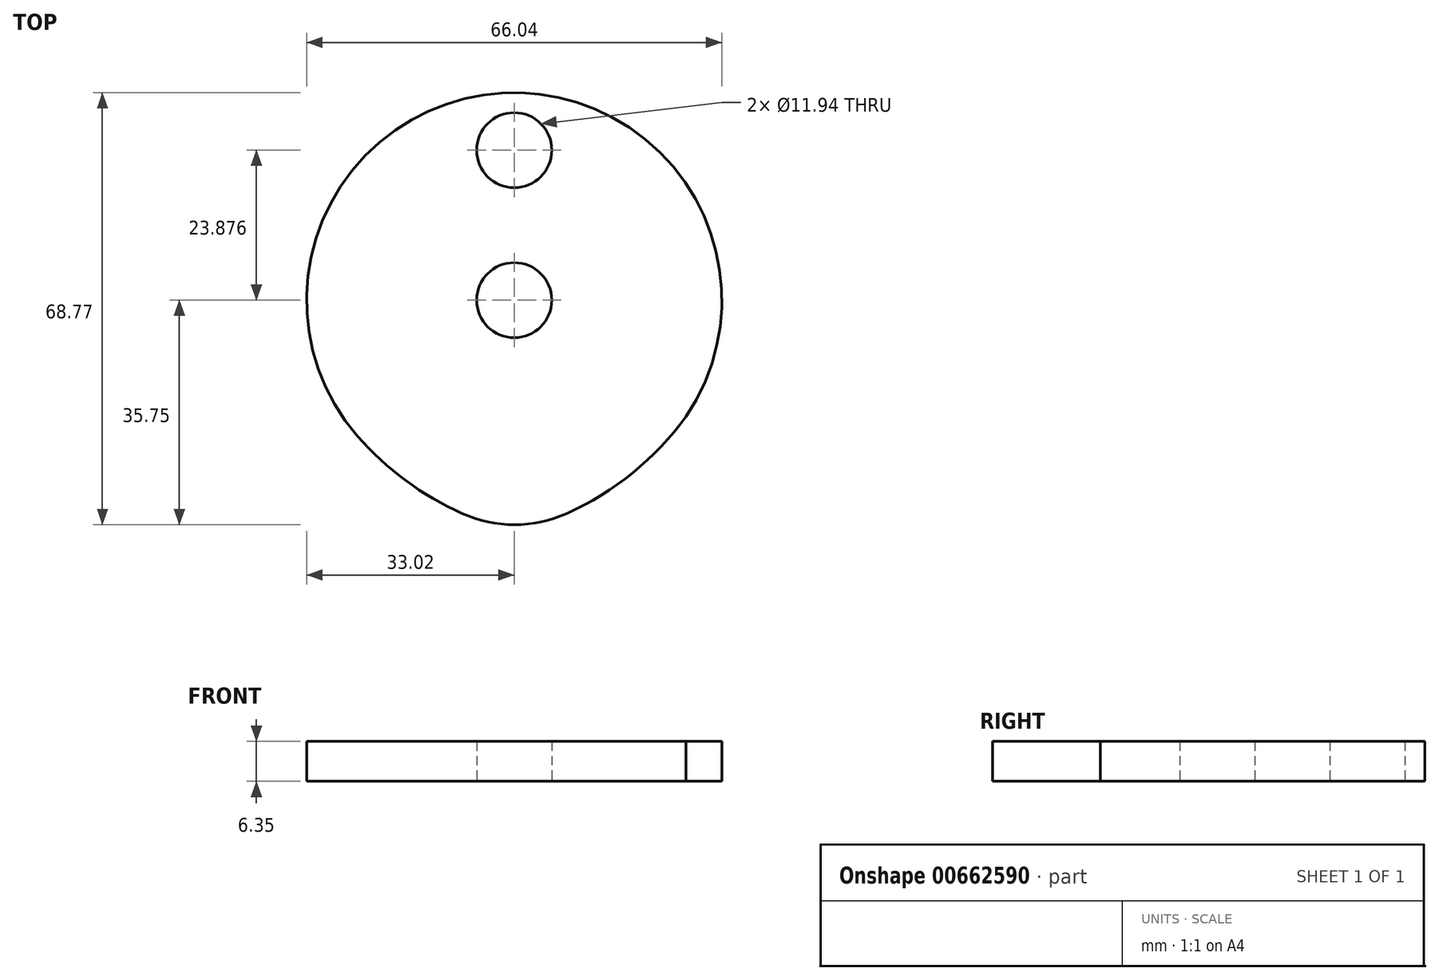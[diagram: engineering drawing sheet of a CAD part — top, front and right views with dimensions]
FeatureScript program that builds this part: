
annotation { "Feature Type Name" : "Feature", "Feature Type Description" : "" }
export const myFeature = defineFeature(function(context is Context, id is Id, definition is map)
    precondition{}
    {
        {
            var Q0;
            Q0=qCreatedBy(makeId("Top.planeOp"),FACE);
            var sketch = newSketch(context, id + "F0", { "sketchPlane" : qUnion([Q0])});
            skArc(sketch, "E0", {"start": v(27.31, -18.56) * mm, "mid": v(-1.96, 32.96) * mm, "end": v(-24.92, -21.66) * mm});
            skLineSegment(sketch, "E1", {"start": v(0, -33.02) * mm, "end": v(0, 23.88) * mm});
            skCircle(sketch, "E2", {"center": v(0, 23.88) * mm, "radius": 5.97 * mm});
            skCircle(sketch, "E3", {"center": v(0, 0) * mm, "radius": 5.97 * mm});
            skLineSegment(sketch, "E4", {"start": v(0, -33.02) * mm, "end": v(0, -36.83) * mm});
            skArc(sketch, "E5", {"start": v(-24.92, -21.66) * mm, "mid": v(-13.62, -31.15) * mm, "end": v(0, -36.83) * mm});
            skArc(sketch, "E6", {"start": v(0, -36.83) * mm, "mid": v(15.3, -30.14) * mm, "end": v(27.31, -18.56) * mm});
            skSolve(sketch);
        }
        {
            var Q0;
            Q0=makeQuery(id+"F0.imprint","IMPRINT",FACE,{"disambiguationData":[TD([[makeQuery(id+"F0.imprint","IMPRINT",EDGE,{"derivedFrom":sQuery(id+"F0.wireOp",EDGE,"E0")}),1.0]])]});
            extrude(context, id + "F1", {"entities" : qUnion([Q0]), "depth" : 6.35 * mm, "offsetDistance" : 25.4 * mm});
        }
        {
            var Q0;
            Q0=makeQuery(id+"F1.opExtrude","SWEPT_EDGE",EDGE,{"disambiguationData":[OSD([sQuery(id+"F0.wireOp",EDGE,"E5"),sQuery(id+"F0.wireOp",EDGE,"E6")])]});
            fillet(context, id + "F2", {"entities" : qUnion([Q0]), "radius" : 20.32 * mm, "tangentPropagation" : true, "allowEdgeOverflow" : false});
        }
    });
